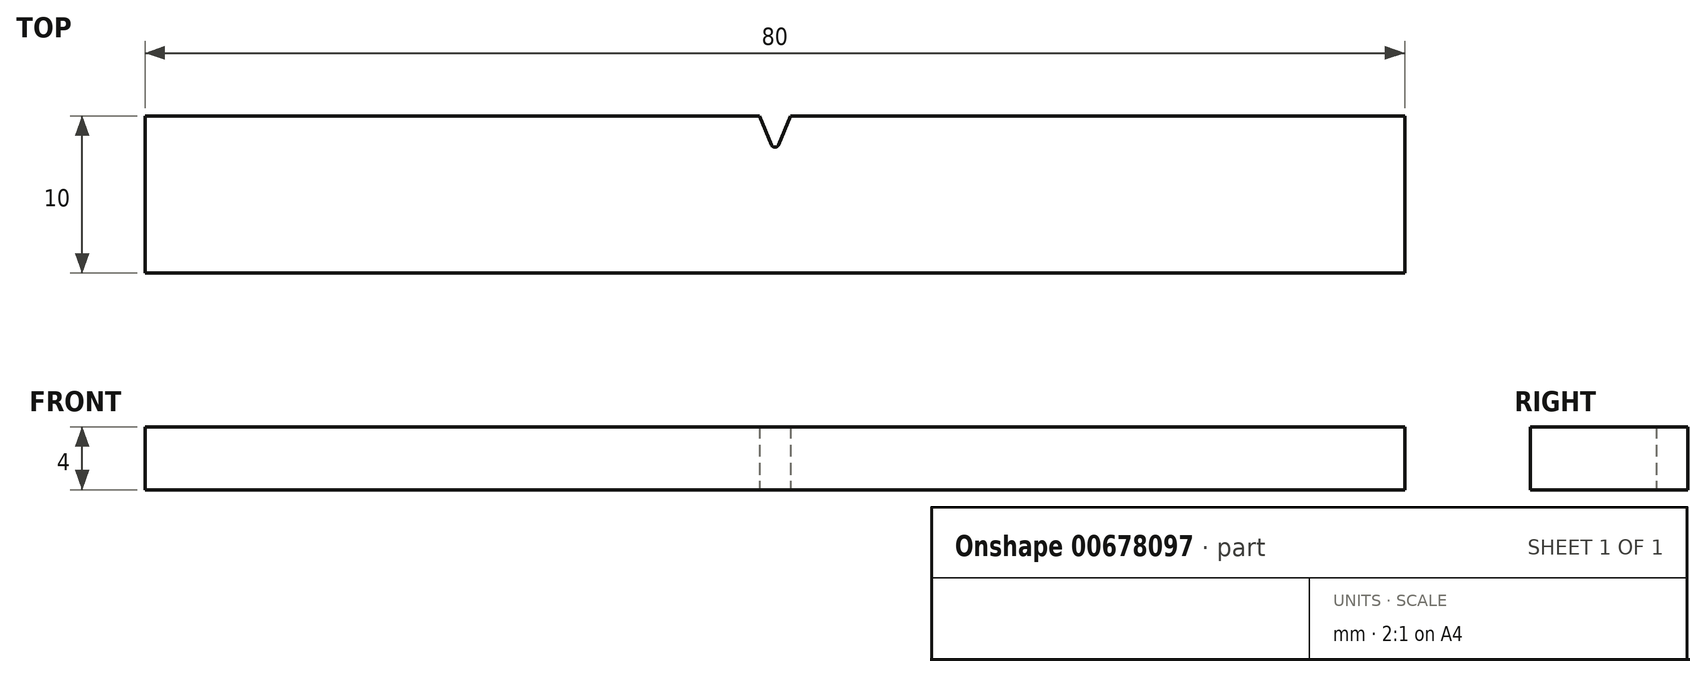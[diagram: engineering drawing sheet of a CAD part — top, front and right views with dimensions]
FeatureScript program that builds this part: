
annotation { "Feature Type Name" : "Feature", "Feature Type Description" : "" }
export const myFeature = defineFeature(function(context is Context, id is Id, definition is map)
    precondition{}
    {
        {
            var Q0;
            Q0=qCreatedBy(makeId("Top.planeOp"),FACE);
            var sketch = newSketch(context, id + "F0", { "sketchPlane" : qUnion([Q0])});
            skLineSegment(sketch, "E0", {"start": v(0, 10) * mm, "end": v(0, 0) * mm});
            skLineSegment(sketch, "E1", {"start": v(0, 0) * mm, "end": v(-80, 0) * mm});
            skLineSegment(sketch, "E2", {"start": v(-80, 0) * mm, "end": v(-80, 10) * mm});
            skArc(sketch, "E3", {"start": v(-40.22, 8.15) * mm, "mid": v(-40, 8) * mm, "end": v(-39.76, 8.15) * mm});
            skLineSegment(sketch, "E4", {"start": v(-39, 10) * mm, "end": v(-39.76, 8.15) * mm});
            skLineSegment(sketch, "E5", {"start": v(-40.99, 10) * mm, "end": v(-40.22, 8.15) * mm});
            skLineSegment(sketch, "E6", {"start": v(-40.99, 10) * mm, "end": v(-80, 10) * mm});
            skLineSegment(sketch, "E7", {"start": v(-39, 10) * mm, "end": v(0, 10) * mm});
            skPoint(sketch, "E8.start.orphan", {"position": v(-40, 0) * mm});
            skSolve(sketch);
        }
        {
            var Q0;
            Q0=makeQuery(id+"F0.imprint","IMPRINT",FACE,{"disambiguationData":[TD([[makeQuery(id+"F0.imprint","IMPRINT",EDGE,{"derivedFrom":sQuery(id+"F0.wireOp",EDGE,"E0")}),-1.0]])]});
            extrude(context, id + "F1", {"entities" : qUnion([Q0]), "depth" : 4 * mm, "offsetDistance" : 25 * mm});
        }
    });
